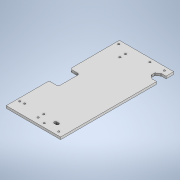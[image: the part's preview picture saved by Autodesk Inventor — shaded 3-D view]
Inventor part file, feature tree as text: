
AUTODESK INVENTOR PART (.ipt)
format: ipt  version: 2021 (Build 250183000, 183)  size: 209,920 bytes
history: native  units: mm
features: sketch x8, extrude x4, hole x4, fillet x3
ambient origin geometry x8: Origin, YZ Plane, XZ Plane, XY Plane, X Axis, Y Axis, Z Axis, Center Point
bodies: Solid1 (feature_tree)
feature tree (19):
  extrude  "Extrusion1"  Depth=242.0mm
  hole  "Hole1"  [1 undecoded]
  extrude  "Extrusion2"  Depth=12.0mm
  fillet  "Fillet1"  Radius=31.0mm
  hole  "Hole2"  [1 undecoded]
  hole  "Hole3"  [1 undecoded]
  hole  "Hole4"  [1 undecoded]
  extrude  "Extrusion3"  Depth=2.0mm
  extrude  "Extrusion4"  Depth=2.0mm
  fillet  "Fillet2"  Radius=12.0mm
  fillet  "Fillet3"  Radius=31.0mm
  sketch  "Sketch1"  dims[d0=116.2mm d1=242.0mm]
  sketch  "Sketch2"  dims[d2=5.0mm d3=0.0mm d4=8.0mm]
  sketch  "Sketch3"  dims[d5=8.0mm d6=12.0mm d7=31.0mm]
  sketch  "Sketch4"  dims[d8=3.8mm d9=6.0mm d10=4.0mm d11=2.0mm d12=90.0deg d13=8.0mm d14=20.594885mm d15=26.5mm]
  sketch  "Sketch5"  dims[d16=20.0mm d17=18.0mm]
  sketch  "Sketch6"  dims[d18=8.0mm d19=10.0mm]
  sketch  "Sketch7"  dims[d20=0.0mm d21=0.0mm d22=2.0mm]
  sketch  "Sketch8"  dims[d24=12.0mm d25=12.0mm d26=12.0mm d27=31.0mm d28=3.8mm d29=6.0mm d30=4.0mm d31=2.0mm d32=90.0deg d33=8.0mm d34=20.594885mm d35=32.0mm d36=60.0mm d37=16.0mm d38=23.25mm d39=3.8mm d40=6.0mm d41=4.0mm d42=2.0mm d43=90.0deg d44=8.0mm d45=20.594885mm d46=6.5mm d47=8.0mm d48=211.75mm d49=3.8mm d50=6.0mm d51=4.0mm d52=2.0mm d53=90.0deg d54=8.0mm d55=20.594885mm d56=21.0mm d57=7.0mm d58=6.0mm d59=25.0mm d60=10.0mm d61=0.0mm d62=2.5mm d63=114.0mm d64=40.0mm d65=45.0mm d66=0.0mm d67=0.0mm d68=4.0mm d69=2.0mm]
note: 4 required parameter values undecoded (feature->parameter linkage not recoverable at this tier; creation-order binding heuristic only, values carry confidence <= 0.55)
